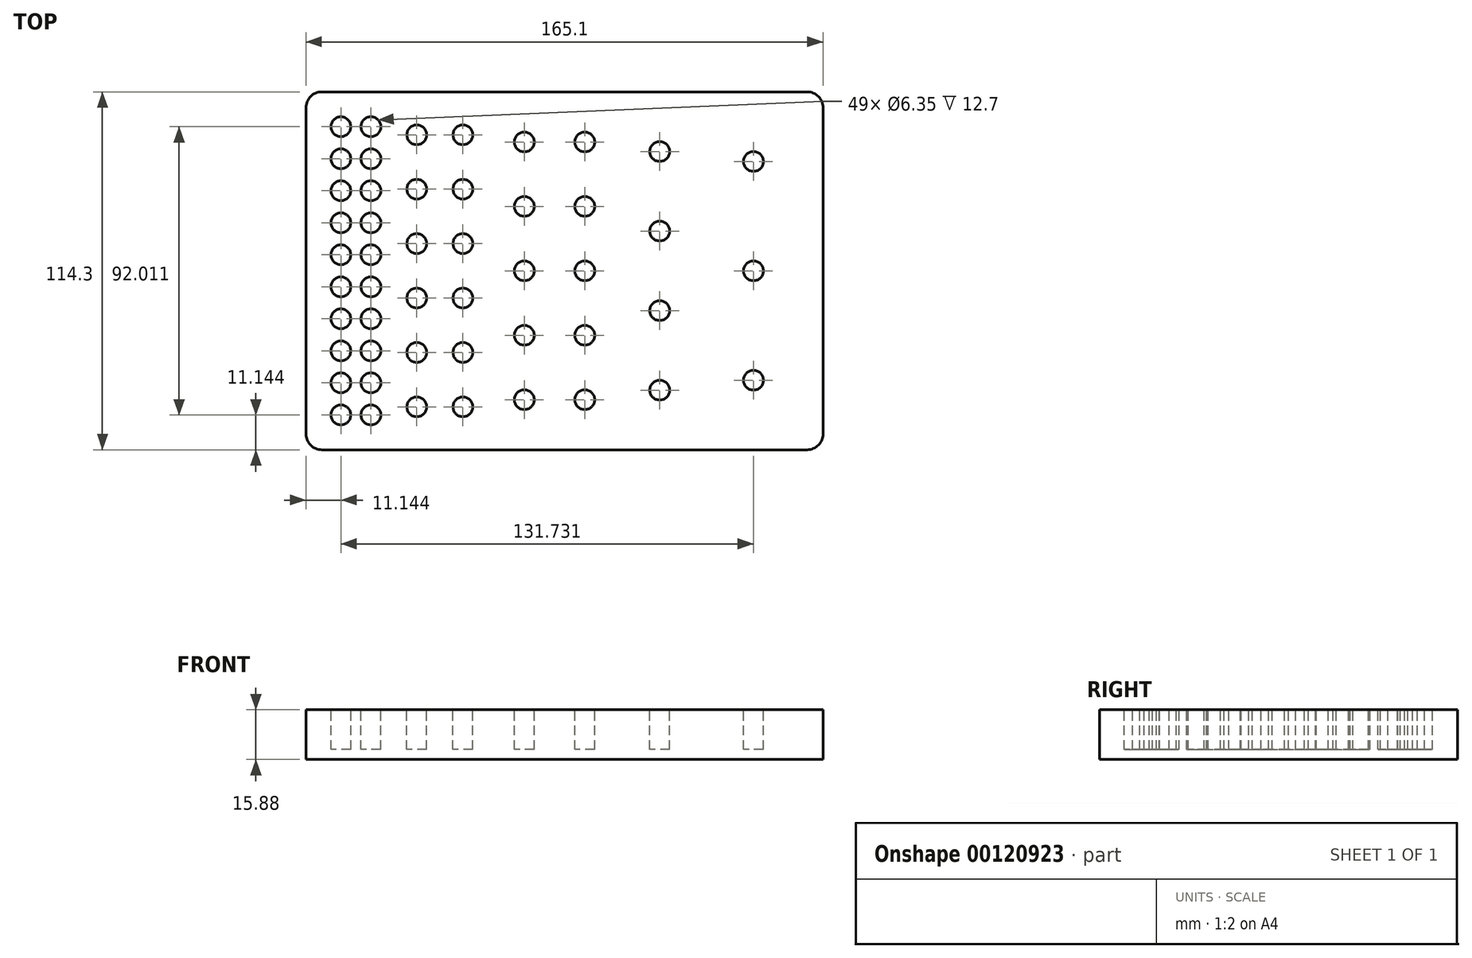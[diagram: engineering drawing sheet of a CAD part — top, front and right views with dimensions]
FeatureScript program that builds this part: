
annotation { "Feature Type Name" : "Feature", "Feature Type Description" : "" }
export const myFeature = defineFeature(function(context is Context, id is Id, definition is map)
    precondition{}
    {
        {
            var Q0;
            Q0=qCreatedBy(makeId("Top.planeOp"),FACE);
            var sketch = newSketch(context, id + "F0", { "sketchPlane" : qUnion([Q0])});
            skLineSegment(sketch, "E0.bottom", {"start": v(-82.55, 57.15) * mm, "end": v(82.55, 57.15) * mm});
            skLineSegment(sketch, "E0.top", {"start": v(-82.55, -57.15) * mm, "end": v(82.55, -57.15) * mm});
            skLineSegment(sketch, "E0.left", {"start": v(-82.55, 57.15) * mm, "end": v(-82.55, -57.15) * mm});
            skLineSegment(sketch, "E0.right", {"start": v(82.55, 57.15) * mm, "end": v(82.55, -57.15) * mm});
            skPoint(sketch, "E0.middle", {"position": v(0, 0) * mm});
            skLineSegment(sketch, "E1", {"start": v(0, 57.15) * mm, "end": v(0, -57.15) * mm, "construction": true});
            skCircle(sketch, "E2", {"center": v(-71.4, -46) * mm, "radius": 3.18 * mm});
            skCircle(sketch, "E3", {"center": v(-71.4, -46) * mm, "radius": 4.8 * mm, "construction": true});
            skCircle(sketch, "E4", {"center": v(-47.17, -43.43) * mm, "radius": 3.18 * mm});
            skCircle(sketch, "E5", {"center": v(-47.17, -43.43) * mm, "radius": 7.37 * mm, "construction": true});
            skCircle(sketch, "E6", {"center": v(-12.84, -41.15) * mm, "radius": 3.18 * mm});
            skCircle(sketch, "E7", {"center": v(-12.84, -41.15) * mm, "radius": 9.65 * mm, "construction": true});
            skCircle(sketch, "E8", {"center": v(30.4, -38.1) * mm, "radius": 3.18 * mm});
            skCircle(sketch, "E9", {"center": v(30.4, -38.1) * mm, "radius": 12.7 * mm, "construction": true});
            skCircle(sketch, "E10", {"center": v(60.33, -34.92) * mm, "radius": 3.18 * mm});
            skCircle(sketch, "E11", {"center": v(60.33, -34.92) * mm, "radius": 15.88 * mm, "construction": true});
            skLineSegment(sketch, "E12.0", {"start": v(-76.2, 50.8) * mm, "end": v(76.2, 50.8) * mm, "construction": true});
            skLineSegment(sketch, "E12.1", {"start": v(-76.2, 50.8) * mm, "end": v(-76.2, -50.8) * mm, "construction": true});
            skLineSegment(sketch, "E12.2", {"start": v(-76.2, -50.8) * mm, "end": v(76.2, -50.8) * mm, "construction": true});
            skLineSegment(sketch, "E12.3", {"start": v(76.2, 50.8) * mm, "end": v(76.2, -50.8) * mm, "construction": true});
            skCircle(sketch, "E13.0.1.0", {"center": v(-71.4, -35.78) * mm, "radius": 3.18 * mm});
            skCircle(sketch, "E13.0.1.1", {"center": v(-71.4, -35.78) * mm, "radius": 4.8 * mm, "construction": true});
            skCircle(sketch, "E13.0.2.0", {"center": v(-71.4, -25.56) * mm, "radius": 3.18 * mm});
            skCircle(sketch, "E13.0.2.1", {"center": v(-71.4, -25.56) * mm, "radius": 4.8 * mm, "construction": true});
            skCircle(sketch, "E13.0.3.0", {"center": v(-71.4, -15.34) * mm, "radius": 3.18 * mm});
            skCircle(sketch, "E13.0.3.1", {"center": v(-71.4, -15.34) * mm, "radius": 4.8 * mm, "construction": true});
            skCircle(sketch, "E13.0.4.0", {"center": v(-71.4, -5.11) * mm, "radius": 3.18 * mm});
            skCircle(sketch, "E13.0.4.1", {"center": v(-71.4, -5.11) * mm, "radius": 4.8 * mm, "construction": true});
            skCircle(sketch, "E13.0.5.0", {"center": v(-71.4, 5.11) * mm, "radius": 3.18 * mm});
            skCircle(sketch, "E13.0.5.1", {"center": v(-71.4, 5.11) * mm, "radius": 4.8 * mm, "construction": true});
            skCircle(sketch, "E13.0.6.0", {"center": v(-71.4, 15.34) * mm, "radius": 3.18 * mm});
            skCircle(sketch, "E13.0.6.1", {"center": v(-71.4, 15.34) * mm, "radius": 4.8 * mm, "construction": true});
            skLineSegment(sketch, "E13.direction1", {"start": v(-71.4, -46) * mm, "end": v(-61.82, -46) * mm, "construction": true});
            skLineSegment(sketch, "E13.direction2", {"start": v(-71.4, -46) * mm, "end": v(-71.4, -35.78) * mm, "construction": true});
            skCircle(sketch, "E14.0.1.0", {"center": v(-47.17, -26.06) * mm, "radius": 3.18 * mm});
            skCircle(sketch, "E14.0.1.1", {"center": v(-47.17, -26.06) * mm, "radius": 7.37 * mm, "construction": true});
            skCircle(sketch, "E14.0.2.0", {"center": v(-47.17, -8.69) * mm, "radius": 3.18 * mm});
            skCircle(sketch, "E14.0.2.1", {"center": v(-47.17, -8.69) * mm, "radius": 7.37 * mm, "construction": true});
            skCircle(sketch, "E14.0.3.0", {"center": v(-47.17, 8.69) * mm, "radius": 3.18 * mm});
            skCircle(sketch, "E14.0.3.1", {"center": v(-47.17, 8.69) * mm, "radius": 7.37 * mm, "construction": true});
            skCircle(sketch, "E14.0.4.0", {"center": v(-47.17, 26.06) * mm, "radius": 3.18 * mm});
            skCircle(sketch, "E14.0.4.1", {"center": v(-47.17, 26.06) * mm, "radius": 7.37 * mm, "construction": true});
            skLineSegment(sketch, "E14.direction1", {"start": v(-47.17, -43.43) * mm, "end": v(-32.44, -43.43) * mm, "construction": true});
            skLineSegment(sketch, "E14.direction2", {"start": v(-47.17, -43.43) * mm, "end": v(-47.17, -26.06) * mm, "construction": true});
            skCircle(sketch, "E15.0.1.0", {"center": v(-12.84, -20.57) * mm, "radius": 9.65 * mm, "construction": true});
            skCircle(sketch, "E15.0.1.1", {"center": v(-12.84, -20.57) * mm, "radius": 3.18 * mm});
            skCircle(sketch, "E15.0.2.0", {"center": v(-12.84, 0) * mm, "radius": 9.65 * mm, "construction": true});
            skCircle(sketch, "E15.0.2.1", {"center": v(-12.84, 0) * mm, "radius": 3.18 * mm});
            skCircle(sketch, "E15.0.3.0", {"center": v(-12.84, 20.57) * mm, "radius": 9.65 * mm, "construction": true});
            skCircle(sketch, "E15.0.3.1", {"center": v(-12.84, 20.57) * mm, "radius": 3.18 * mm});
            skCircle(sketch, "E15.0.4.0", {"center": v(-12.84, 41.15) * mm, "radius": 9.65 * mm, "construction": true});
            skCircle(sketch, "E15.0.4.1", {"center": v(-12.84, 41.15) * mm, "radius": 3.18 * mm});
            skLineSegment(sketch, "E15.direction1", {"start": v(-12.84, -41.15) * mm, "end": v(6.46, -41.15) * mm, "construction": true});
            skLineSegment(sketch, "E15.direction2", {"start": v(-12.84, -41.15) * mm, "end": v(-12.84, -20.57) * mm, "construction": true});
            skCircle(sketch, "E16.0.1.0", {"center": v(30.4, -12.7) * mm, "radius": 3.18 * mm});
            skCircle(sketch, "E16.0.1.1", {"center": v(30.4, -12.7) * mm, "radius": 12.7 * mm, "construction": true});
            skCircle(sketch, "E16.0.2.0", {"center": v(30.4, 12.7) * mm, "radius": 3.18 * mm});
            skCircle(sketch, "E16.0.2.1", {"center": v(30.4, 12.7) * mm, "radius": 12.7 * mm, "construction": true});
            skCircle(sketch, "E16.0.3.0", {"center": v(30.4, 38.1) * mm, "radius": 3.18 * mm});
            skCircle(sketch, "E16.0.3.1", {"center": v(30.4, 38.1) * mm, "radius": 12.7 * mm, "construction": true});
            skLineSegment(sketch, "E16.direction1", {"start": v(30.4, -38.1) * mm, "end": v(41.94, -38.1) * mm, "construction": true});
            skLineSegment(sketch, "E16.direction2", {"start": v(30.4, -38.1) * mm, "end": v(30.4, -12.7) * mm, "construction": true});
            skCircle(sketch, "E17.0.1.0", {"center": v(60.33, 0) * mm, "radius": 15.88 * mm, "construction": true});
            skCircle(sketch, "E17.0.1.1", {"center": v(60.33, 0) * mm, "radius": 3.18 * mm});
            skCircle(sketch, "E17.0.2.0", {"center": v(60.33, 34.93) * mm, "radius": 15.88 * mm, "construction": true});
            skCircle(sketch, "E17.0.2.1", {"center": v(60.33, 34.93) * mm, "radius": 3.18 * mm});
            skLineSegment(sketch, "E17.direction1", {"start": v(60.33, -34.92) * mm, "end": v(72.62, -34.92) * mm, "construction": true});
            skLineSegment(sketch, "E17.direction2", {"start": v(60.33, -34.92) * mm, "end": v(60.33, 0) * mm, "construction": true});
            skCircle(sketch, "E18.0.0.5", {"center": v(-47.17, 43.43) * mm, "radius": 3.18 * mm});
            skCircle(sketch, "E18.2.0.5", {"center": v(-47.17, 43.43) * mm, "radius": 7.37 * mm, "construction": true});
            skCircle(sketch, "E19.0.0.7", {"center": v(-71.4, 25.56) * mm, "radius": 3.18 * mm});
            skCircle(sketch, "E19.2.0.7", {"center": v(-71.4, 25.56) * mm, "radius": 4.8 * mm, "construction": true});
            skCircle(sketch, "E19.0.0.8", {"center": v(-71.4, 35.78) * mm, "radius": 3.18 * mm});
            skCircle(sketch, "E19.2.0.8", {"center": v(-71.4, 35.78) * mm, "radius": 4.8 * mm, "construction": true});
            skCircle(sketch, "E20.0.0.9", {"center": v(-71.4, 46) * mm, "radius": 3.18 * mm});
            skCircle(sketch, "E20.2.0.9", {"center": v(-71.4, 46) * mm, "radius": 4.8 * mm, "construction": true});
            skCircle(sketch, "E21.0.1.0", {"center": v(-61.82, -46) * mm, "radius": 3.18 * mm});
            skCircle(sketch, "E21.2.1.0", {"center": v(-61.82, -46) * mm, "radius": 4.8 * mm, "construction": true});
            skCircle(sketch, "E21.0.1.1", {"center": v(-61.82, -35.78) * mm, "radius": 3.18 * mm});
            skCircle(sketch, "E21.2.1.1", {"center": v(-61.82, -35.78) * mm, "radius": 4.8 * mm, "construction": true});
            skCircle(sketch, "E21.0.1.2", {"center": v(-61.82, -25.56) * mm, "radius": 3.18 * mm});
            skCircle(sketch, "E21.2.1.2", {"center": v(-61.82, -25.56) * mm, "radius": 4.8 * mm, "construction": true});
            skCircle(sketch, "E21.0.1.3", {"center": v(-61.82, -15.34) * mm, "radius": 3.18 * mm});
            skCircle(sketch, "E21.2.1.3", {"center": v(-61.82, -15.34) * mm, "radius": 4.8 * mm, "construction": true});
            skCircle(sketch, "E21.0.1.4", {"center": v(-61.82, -5.11) * mm, "radius": 3.18 * mm});
            skCircle(sketch, "E21.2.1.4", {"center": v(-61.82, -5.11) * mm, "radius": 4.8 * mm, "construction": true});
            skCircle(sketch, "E21.0.1.5", {"center": v(-61.82, 5.11) * mm, "radius": 3.18 * mm});
            skCircle(sketch, "E21.2.1.5", {"center": v(-61.82, 5.11) * mm, "radius": 4.8 * mm, "construction": true});
            skCircle(sketch, "E21.0.1.6", {"center": v(-61.82, 15.34) * mm, "radius": 3.18 * mm});
            skCircle(sketch, "E21.2.1.6", {"center": v(-61.82, 15.34) * mm, "radius": 4.8 * mm, "construction": true});
            skCircle(sketch, "E21.0.1.7", {"center": v(-61.82, 25.56) * mm, "radius": 3.18 * mm});
            skCircle(sketch, "E21.2.1.7", {"center": v(-61.82, 25.56) * mm, "radius": 4.8 * mm, "construction": true});
            skCircle(sketch, "E21.0.1.8", {"center": v(-61.82, 35.78) * mm, "radius": 3.18 * mm});
            skCircle(sketch, "E21.2.1.8", {"center": v(-61.82, 35.78) * mm, "radius": 4.8 * mm, "construction": true});
            skCircle(sketch, "E21.0.1.9", {"center": v(-61.82, 46) * mm, "radius": 3.18 * mm});
            skCircle(sketch, "E21.2.1.9", {"center": v(-61.82, 46) * mm, "radius": 4.8 * mm, "construction": true});
            skCircle(sketch, "E22.0.1.0", {"center": v(-32.44, -43.43) * mm, "radius": 3.18 * mm});
            skCircle(sketch, "E22.2.1.0", {"center": v(-32.44, -43.43) * mm, "radius": 7.37 * mm, "construction": true});
            skCircle(sketch, "E22.0.1.1", {"center": v(-32.44, -26.06) * mm, "radius": 3.18 * mm});
            skCircle(sketch, "E22.2.1.1", {"center": v(-32.44, -26.06) * mm, "radius": 7.37 * mm, "construction": true});
            skCircle(sketch, "E22.0.1.2", {"center": v(-32.44, -8.69) * mm, "radius": 3.18 * mm});
            skCircle(sketch, "E22.2.1.2", {"center": v(-32.44, -8.69) * mm, "radius": 7.37 * mm, "construction": true});
            skCircle(sketch, "E22.0.1.3", {"center": v(-32.44, 8.69) * mm, "radius": 3.18 * mm});
            skCircle(sketch, "E22.2.1.3", {"center": v(-32.44, 8.69) * mm, "radius": 7.37 * mm, "construction": true});
            skCircle(sketch, "E22.0.1.4", {"center": v(-32.44, 26.06) * mm, "radius": 3.18 * mm});
            skCircle(sketch, "E22.2.1.4", {"center": v(-32.44, 26.06) * mm, "radius": 7.37 * mm, "construction": true});
            skCircle(sketch, "E22.0.1.5", {"center": v(-32.44, 43.43) * mm, "radius": 3.18 * mm});
            skCircle(sketch, "E22.2.1.5", {"center": v(-32.44, 43.43) * mm, "radius": 7.37 * mm, "construction": true});
            skCircle(sketch, "E23.0.1.0", {"center": v(6.46, -41.15) * mm, "radius": 9.65 * mm, "construction": true});
            skCircle(sketch, "E23.2.1.0", {"center": v(6.46, -41.15) * mm, "radius": 3.18 * mm});
            skCircle(sketch, "E23.0.1.1", {"center": v(6.46, -20.57) * mm, "radius": 9.65 * mm, "construction": true});
            skCircle(sketch, "E23.2.1.1", {"center": v(6.46, -20.57) * mm, "radius": 3.18 * mm});
            skCircle(sketch, "E23.0.1.2", {"center": v(6.46, 0) * mm, "radius": 9.65 * mm, "construction": true});
            skCircle(sketch, "E23.2.1.2", {"center": v(6.46, 0) * mm, "radius": 3.18 * mm});
            skCircle(sketch, "E23.0.1.3", {"center": v(6.46, 20.57) * mm, "radius": 9.65 * mm, "construction": true});
            skCircle(sketch, "E23.2.1.3", {"center": v(6.46, 20.57) * mm, "radius": 3.18 * mm});
            skCircle(sketch, "E23.0.1.4", {"center": v(6.46, 41.15) * mm, "radius": 9.65 * mm, "construction": true});
            skCircle(sketch, "E23.2.1.4", {"center": v(6.46, 41.15) * mm, "radius": 3.18 * mm});
            skSolve(sketch);
        }
        {
            var Q0;
            Q0=makeQuery(id+"F0.imprint","IMPRINT",FACE,{"disambiguationData":[TD([[makeQuery(id+"F0.imprint","IMPRINT",EDGE,{"derivedFrom":sQuery(id+"F0.wireOp",EDGE,"E0.bottom")}),-1.0]])]});
            extrude(context, id + "F1", {"entities" : qUnion([Q0]), "oppositeDirection" : true, "depth" : 12.7 * mm});
        }
        {
            var Q0;
            Q0=makeQuery(id+"F1.opExtrude","CAP_FACE",FACE,{"disambiguationData":[OSD([sQuery(id+"F0.wireOp",EDGE,"E0.bottom"),sQuery(id+"F0.wireOp",EDGE,"E0.top"),sQuery(id+"F0.wireOp",EDGE,"E0.left"),sQuery(id+"F0.wireOp",EDGE,"E0.right"),sQuery(id+"F0.wireOp",EDGE,"E2"),sQuery(id+"F0.wireOp",EDGE,"E4"),sQuery(id+"F0.wireOp",EDGE,"E6"),sQuery(id+"F0.wireOp",EDGE,"E8"),sQuery(id+"F0.wireOp",EDGE,"E10"),sQuery(id+"F0.wireOp",EDGE,"E13.0.1.0"),sQuery(id+"F0.wireOp",EDGE,"E13.0.2.0"),sQuery(id+"F0.wireOp",EDGE,"E13.0.3.0"),sQuery(id+"F0.wireOp",EDGE,"E13.0.4.0"),sQuery(id+"F0.wireOp",EDGE,"E13.0.5.0"),sQuery(id+"F0.wireOp",EDGE,"E13.0.6.0"),sQuery(id+"F0.wireOp",EDGE,"E14.0.1.0"),sQuery(id+"F0.wireOp",EDGE,"E14.0.2.0"),sQuery(id+"F0.wireOp",EDGE,"E14.0.3.0"),sQuery(id+"F0.wireOp",EDGE,"E14.0.4.0"),sQuery(id+"F0.wireOp",EDGE,"E15.0.1.1"),sQuery(id+"F0.wireOp",EDGE,"E15.0.2.1"),sQuery(id+"F0.wireOp",EDGE,"E15.0.3.1"),sQuery(id+"F0.wireOp",EDGE,"E15.0.4.1"),sQuery(id+"F0.wireOp",EDGE,"E16.0.1.0"),sQuery(id+"F0.wireOp",EDGE,"E16.0.2.0"),sQuery(id+"F0.wireOp",EDGE,"E16.0.3.0"),sQuery(id+"F0.wireOp",EDGE,"E17.0.1.1"),sQuery(id+"F0.wireOp",EDGE,"E17.0.2.1"),sQuery(id+"F0.wireOp",EDGE,"E18.0.0.5"),sQuery(id+"F0.wireOp",EDGE,"E19.0.0.7"),sQuery(id+"F0.wireOp",EDGE,"E19.0.0.8"),sQuery(id+"F0.wireOp",EDGE,"E20.0.0.9"),sQuery(id+"F0.wireOp",EDGE,"E21.0.1.0"),sQuery(id+"F0.wireOp",EDGE,"E21.0.1.1"),sQuery(id+"F0.wireOp",EDGE,"E21.0.1.2"),sQuery(id+"F0.wireOp",EDGE,"E21.0.1.3"),sQuery(id+"F0.wireOp",EDGE,"E21.0.1.4"),sQuery(id+"F0.wireOp",EDGE,"E21.0.1.5"),sQuery(id+"F0.wireOp",EDGE,"E21.0.1.6"),sQuery(id+"F0.wireOp",EDGE,"E21.0.1.7"),sQuery(id+"F0.wireOp",EDGE,"E21.0.1.8"),sQuery(id+"F0.wireOp",EDGE,"E21.0.1.9"),sQuery(id+"F0.wireOp",EDGE,"E22.0.1.0"),sQuery(id+"F0.wireOp",EDGE,"E22.0.1.1"),sQuery(id+"F0.wireOp",EDGE,"E22.0.1.2"),sQuery(id+"F0.wireOp",EDGE,"E22.0.1.3"),sQuery(id+"F0.wireOp",EDGE,"E22.0.1.4"),sQuery(id+"F0.wireOp",EDGE,"E22.0.1.5"),sQuery(id+"F0.wireOp",EDGE,"E23.2.1.0"),sQuery(id+"F0.wireOp",EDGE,"E23.2.1.1"),sQuery(id+"F0.wireOp",EDGE,"E23.2.1.2"),sQuery(id+"F0.wireOp",EDGE,"E23.2.1.3"),sQuery(id+"F0.wireOp",EDGE,"E23.2.1.4")])],"isStart":false});
            var sketch = newSketch(context, id + "F2", { "sketchPlane" : qUnion([Q0])});
            skLineSegment(sketch, "E24.bottom", {"start": v(-82.55, 57.15) * mm, "end": v(82.55, 57.15) * mm});
            skLineSegment(sketch, "E24.top", {"start": v(-82.55, -57.15) * mm, "end": v(82.55, -57.15) * mm});
            skLineSegment(sketch, "E24.left", {"start": v(-82.55, 57.15) * mm, "end": v(-82.55, -57.15) * mm});
            skLineSegment(sketch, "E24.right", {"start": v(82.55, 57.15) * mm, "end": v(82.55, -57.15) * mm});
            skSolve(sketch);
        }
        {
            var Q0;
            Q0 = qSketchRegion(id + "F2", true);
            extrude(context, id + "F3", {"entities" : qUnion([Q0]), "operationType" : NewBodyOperationType.ADD, "depth" : 3.17 * mm});
        }
        {
            var Q0;
            Q0=makeQuery(id+"F3.boolean.opBoolean","MERGE",EDGE,{"derivedFrom":[makeQuery(id+"F1.opExtrude","SWEPT_EDGE",EDGE,{"disambiguationData":[OSD([sQuery(id+"F0.wireOp",EDGE,"E0.top"),sQuery(id+"F0.wireOp",EDGE,"E0.left")])]}),makeQuery(id+"F3.opExtrude","SWEPT_EDGE",EDGE,{"disambiguationData":[OSD([sQuery(id+"F2.wireOp",EDGE,"E24.bottom"),sQuery(id+"F2.wireOp",EDGE,"E24.left")])]})]});
            var Q1;
            Q1=makeQuery(id+"F3.boolean.opBoolean","MERGE",EDGE,{"derivedFrom":[makeQuery(id+"F1.opExtrude","SWEPT_EDGE",EDGE,{"disambiguationData":[OSD([sQuery(id+"F0.wireOp",EDGE,"E0.bottom"),sQuery(id+"F0.wireOp",EDGE,"E0.left")])]}),makeQuery(id+"F3.opExtrude","SWEPT_EDGE",EDGE,{"disambiguationData":[OSD([sQuery(id+"F2.wireOp",EDGE,"E24.top"),sQuery(id+"F2.wireOp",EDGE,"E24.left")])]})]});
            var Q2;
            Q2=makeQuery(id+"F3.boolean.opBoolean","MERGE",EDGE,{"derivedFrom":[makeQuery(id+"F1.opExtrude","SWEPT_EDGE",EDGE,{"disambiguationData":[OSD([sQuery(id+"F0.wireOp",EDGE,"E0.top"),sQuery(id+"F0.wireOp",EDGE,"E0.right")])]}),makeQuery(id+"F3.opExtrude","SWEPT_EDGE",EDGE,{"disambiguationData":[OSD([sQuery(id+"F2.wireOp",EDGE,"E24.bottom"),sQuery(id+"F2.wireOp",EDGE,"E24.right")])]})]});
            var Q3;
            Q3=makeQuery(id+"F3.boolean.opBoolean","MERGE",EDGE,{"derivedFrom":[makeQuery(id+"F1.opExtrude","SWEPT_EDGE",EDGE,{"disambiguationData":[OSD([sQuery(id+"F0.wireOp",EDGE,"E0.bottom"),sQuery(id+"F0.wireOp",EDGE,"E0.right")])]}),makeQuery(id+"F3.opExtrude","SWEPT_EDGE",EDGE,{"disambiguationData":[OSD([sQuery(id+"F2.wireOp",EDGE,"E24.top"),sQuery(id+"F2.wireOp",EDGE,"E24.right")])]})]});
            fillet(context, id + "F4", {"entities" : qUnion([Q0, Q1, Q2, Q3]), "radius" : 5.08 * mm, "tangentPropagation" : true, "allowEdgeOverflow" : false});
        }
    });
